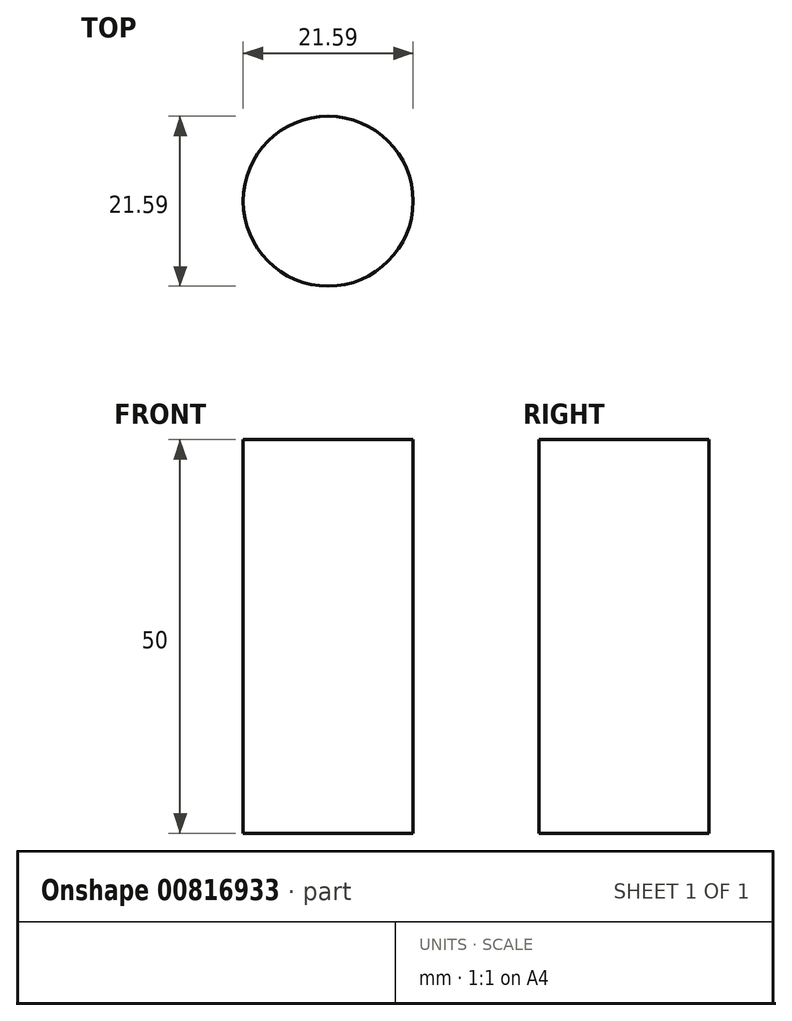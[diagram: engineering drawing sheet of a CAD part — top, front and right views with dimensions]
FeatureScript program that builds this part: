
annotation { "Feature Type Name" : "Feature", "Feature Type Description" : "" }
export const myFeature = defineFeature(function(context is Context, id is Id, definition is map)
    precondition{}
    {
        {
            var Q0;
            Q0=qCreatedBy(makeId("Top.planeOp"),FACE);
            var sketch = newSketch(context, id + "F0", { "sketchPlane" : qUnion([Q0])});
            skCircle(sketch, "E0", {"center": v(-43.6, -43.74) * mm, "radius": 10.8 * mm});
            skSolve(sketch);
        }
        {
            var Q0;
            Q0=sQuery(id+"F0.wireOp",EDGE,"E0");
            extrude(context, id + "F1", {"bodyType" : ToolBodyType.SURFACE, "surfaceEntities" : qUnion([Q0]), "depth" : 50 * mm, "offsetDistance" : 25 * mm});
        }
    });
